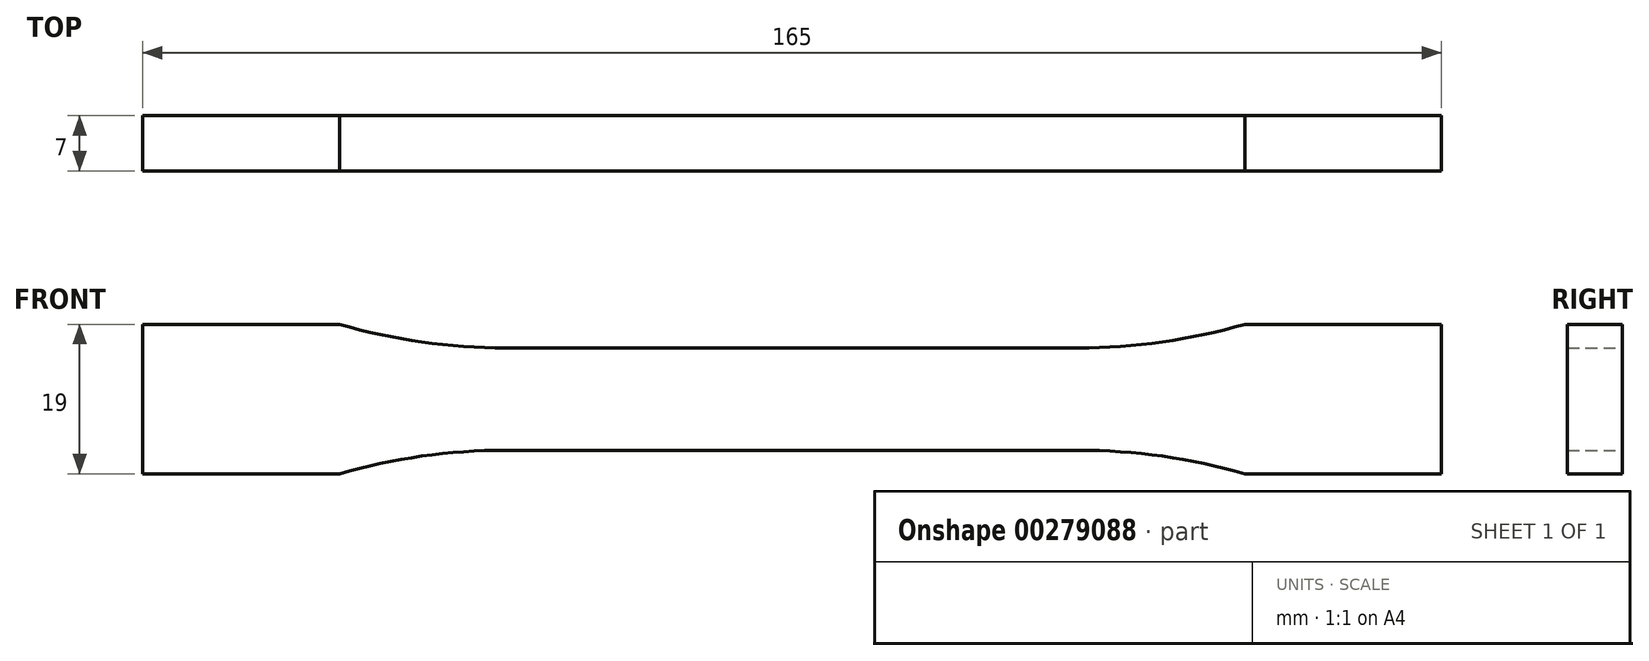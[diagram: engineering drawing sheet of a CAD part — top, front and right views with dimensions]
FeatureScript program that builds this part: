
annotation { "Feature Type Name" : "Feature", "Feature Type Description" : "" }
export const myFeature = defineFeature(function(context is Context, id is Id, definition is map)
    precondition{}
    {
        {
            var Q0;
            Q0=qCreatedBy(makeId("Front.planeOp"),FACE);
            var sketch = newSketch(context, id + "F0", { "sketchPlane" : qUnion([Q0])});
            skLineSegment(sketch, "E0", {"start": v(0, 6.5) * mm, "end": v(36.36, 6.5) * mm});
            skArc(sketch, "E1", {"start": v(36.36, 6.5) * mm, "mid": v(47.03, 7.25) * mm, "end": v(57.5, 9.5) * mm});
            skLineSegment(sketch, "E2", {"start": v(57.5, 9.5) * mm, "end": v(82.5, 9.5) * mm});
            skLineSegment(sketch, "E3.MirrorCS", {"start": v(0, -6.5) * mm, "end": v(36.36, -6.5) * mm});
            skLineSegment(sketch, "E4.MirrorCS", {"start": v(57.5, -9.5) * mm, "end": v(82.5, -9.5) * mm});
            skArc(sketch, "E5.MirrorCS", {"start": v(36.36, -6.5) * mm, "mid": v(47.03, -7.25) * mm, "end": v(57.5, -9.5) * mm});
            skLineSegment(sketch, "E6.MirrorCS", {"start": v(0, 6.5) * mm, "end": v(-36.36, 6.5) * mm});
            skArc(sketch, "E7.MirrorCS", {"start": v(-36.36, 6.5) * mm, "mid": v(-47.03, 7.25) * mm, "end": v(-57.5, 9.5) * mm});
            skLineSegment(sketch, "E8.MirrorCS", {"start": v(-57.5, 9.5) * mm, "end": v(-82.5, 9.5) * mm});
            skLineSegment(sketch, "E9.MirrorCS", {"start": v(0, -6.5) * mm, "end": v(-36.36, -6.5) * mm});
            skLineSegment(sketch, "E10.MirrorCS", {"start": v(-57.5, -9.5) * mm, "end": v(-82.5, -9.5) * mm});
            skArc(sketch, "E11.MirrorCS", {"start": v(-36.36, -6.5) * mm, "mid": v(-47.03, -7.25) * mm, "end": v(-57.5, -9.5) * mm});
            skLineSegment(sketch, "E12", {"start": v(-82.5, 9.5) * mm, "end": v(-82.5, -9.5) * mm});
            skLineSegment(sketch, "E13", {"start": v(82.5, 9.5) * mm, "end": v(82.5, -9.5) * mm});
            skSolve(sketch);
        }
        {
            var Q0;
            Q0=makeQuery(id+"F0.imprint","IMPRINT",FACE,{"disambiguationData":[TD([[makeQuery(id+"F0.imprint","IMPRINT",EDGE,{"derivedFrom":sQuery(id+"F0.wireOp",EDGE,"E1")}),-1.0]])]});
            extrude(context, id + "F1", {"entities" : qUnion([Q0]), "endBound" : BoundingType.SYMMETRIC, "depth" : 7 * mm});
        }
    });
